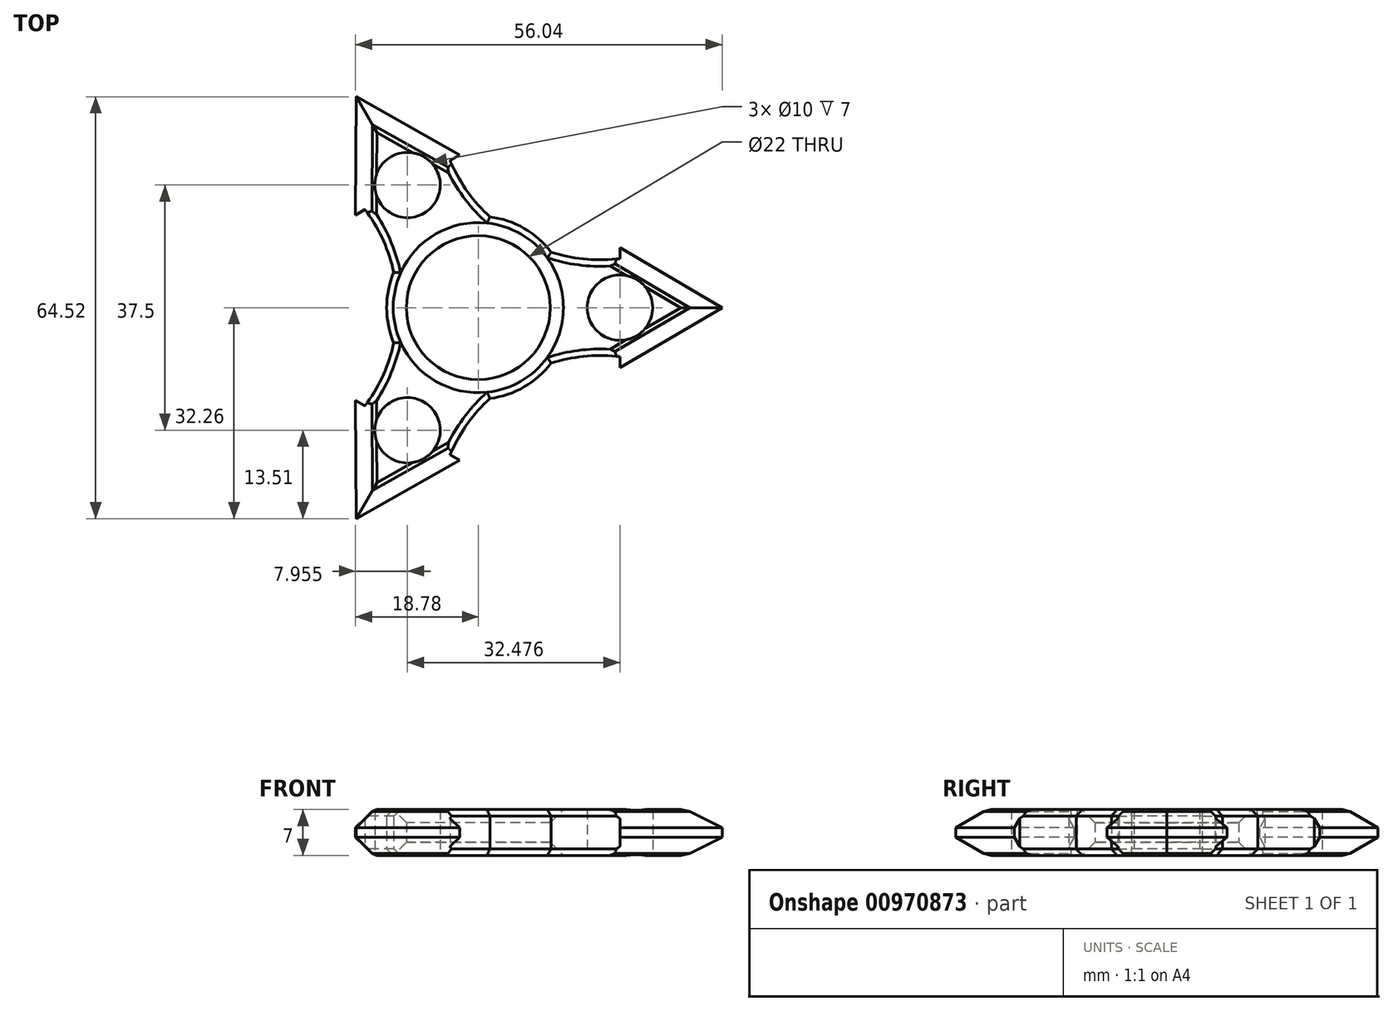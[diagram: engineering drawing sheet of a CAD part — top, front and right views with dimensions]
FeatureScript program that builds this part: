
annotation { "Feature Type Name" : "Feature", "Feature Type Description" : "" }
export const myFeature = defineFeature(function(context is Context, id is Id, definition is map)
    precondition{}
    {
        {
            var Q0;
            Q0=qCreatedBy(makeId("Top.planeOp"),FACE);
            var sketch = newSketch(context, id + "F0", { "sketchPlane" : qUnion([Q0])});
            skCircle(sketch, "E0.cCircle", {"center": v(0, 0) * mm, "radius": 17.32 * mm, "construction": true});
            skPoint(sketch, "E0.0.midPoint", {"position": v(-17.32, 0) * mm});
            skCircle(sketch, "E1", {"center": v(0, 0) * mm, "radius": 11 * mm});
            skLineSegment(sketch, "E2", {"start": v(-17.32, 30) * mm, "end": v(8.66, -15) * mm, "construction": true});
            skLineSegment(sketch, "E3", {"start": v(34.64, 0) * mm, "end": v(-17.32, 0) * mm, "construction": true});
            skLineSegment(sketch, "E4", {"start": v(8.66, 15) * mm, "end": v(-17.32, -30) * mm, "construction": true});
            skArc(sketch, "E5", {"start": v(8.66, 15) * mm, "mid": v(8.66, 15) * mm, "end": v(8.66, 15) * mm});
            skArc(sketch, "E6", {"start": v(-4.33, 22.5) * mm, "mid": v(-1.74, 17.87) * mm, "end": v(1.77, 13.89) * mm});
            skArc(sketch, "E7", {"start": v(-17.32, -15) * mm, "mid": v(-14.6, -10.44) * mm, "end": v(-12.91, -5.4) * mm});
            skArc(sketch, "E8", {"start": v(21.65, -7.5) * mm, "mid": v(16.34, -7.43) * mm, "end": v(11.14, -8.48) * mm});
            skCircle(sketch, "E9", {"center": v(0, 0) * mm, "radius": 14 * mm});
            skLineSegment(sketch, "E10", {"start": v(-10.83, 18.75) * mm, "end": v(-19.33, 33.47) * mm, "construction": true});
            skLineSegment(sketch, "E11", {"start": v(21.65, 0) * mm, "end": v(38.65, 0) * mm, "construction": true});
            skPoint(sketch, "E11.endSnap0", {"position": v(21.65, 0) * mm});
            skLineSegment(sketch, "E12", {"start": v(-10.83, -18.75) * mm, "end": v(-19.33, -33.47) * mm, "construction": true});
            skLineSegment(sketch, "E13", {"start": v(-4.33, 22.5) * mm, "end": v(-2.17, 23.75) * mm, "construction": true});
            skLineSegment(sketch, "E14", {"start": v(-17.32, 15) * mm, "end": v(-19.49, 13.75) * mm, "construction": true});
            skLineSegment(sketch, "E15", {"start": v(-17.32, -15) * mm, "end": v(-19.49, -13.75) * mm, "construction": true});
            skLineSegment(sketch, "E16", {"start": v(-4.33, -22.5) * mm, "end": v(-2.17, -23.75) * mm, "construction": true});
            skLineSegment(sketch, "E17", {"start": v(21.65, -7.5) * mm, "end": v(21.65, -10) * mm, "construction": true});
            skLineSegment(sketch, "E18", {"start": v(21.65, 7.5) * mm, "end": v(21.65, 10) * mm, "construction": true});
            skLineSegment(sketch, "E19", {"start": v(-19.33, 33.47) * mm, "end": v(-19.49, 13.75) * mm});
            skLineSegment(sketch, "E20", {"start": v(-2.17, 23.75) * mm, "end": v(-19.33, 33.47) * mm});
            skLineSegment(sketch, "E21", {"start": v(-19.49, -13.75) * mm, "end": v(-19.33, -33.47) * mm});
            skLineSegment(sketch, "E22", {"start": v(-2.17, -23.75) * mm, "end": v(-19.33, -33.47) * mm});
            skLineSegment(sketch, "E23", {"start": v(-19.49, -13.75) * mm, "end": v(-17.32, -15) * mm});
            skLineSegment(sketch, "E24", {"start": v(21.65, -10) * mm, "end": v(38.65, 0) * mm});
            skLineSegment(sketch, "E25", {"start": v(21.65, 10) * mm, "end": v(38.65, 0) * mm});
            skLineSegment(sketch, "E26", {"start": v(21.65, 10) * mm, "end": v(21.65, 7.5) * mm});
            skLineSegment(sketch, "E27", {"start": v(-19.49, 13.75) * mm, "end": v(-17.32, 15) * mm});
            skPoint(sketch, "E0.2.start.orphan", {"position": v(34.64, 0) * mm});
            skArc(sketch, "E28.trimOffspring", {"start": v(-12.91, 5.4) * mm, "mid": v(-14.6, 10.44) * mm, "end": v(-17.32, 15) * mm});
            skArc(sketch, "E29.trimOffspring", {"start": v(1.77, -13.89) * mm, "mid": v(-1.74, -17.87) * mm, "end": v(-4.33, -22.5) * mm});
            skArc(sketch, "E30.trimOffspring", {"start": v(11.14, 8.48) * mm, "mid": v(16.34, 7.43) * mm, "end": v(21.65, 7.5) * mm});
            skLineSegment(sketch, "E31.trimOffspring", {"start": v(21.65, -7.5) * mm, "end": v(21.65, -10) * mm});
            skLineSegment(sketch, "E32.trimOffspring", {"start": v(-4.33, -22.5) * mm, "end": v(-2.17, -23.75) * mm});
            skLineSegment(sketch, "E33.trimOffspring", {"start": v(-4.33, 22.5) * mm, "end": v(-2.17, 23.75) * mm});
            skCircle(sketch, "E34", {"center": v(-10.83, 18.75) * mm, "radius": 5 * mm});
            skCircle(sketch, "E35", {"center": v(21.65, 0) * mm, "radius": 5 * mm});
            skCircle(sketch, "E36", {"center": v(-10.83, -18.75) * mm, "radius": 5 * mm});
            skSolve(sketch);
        }
        {
            var Q0;
            Q0=qSketchRegion(id+"F0",true);
            extrude(context, id + "F1", {"entities" : qUnion([Q0]), "depth" : 7 * mm, "offsetDistance" : 25 * mm});
        }
        {
            var Q0;
            Q0=makeQuery(id+"F1.opExtrude","CAP_EDGE",EDGE,{"disambiguationData":[OSD([sQuery(id+"F0.wireOp",EDGE,"E24")])],"isStart":false});
            var Q1;
            Q1=makeQuery(id+"F1.opExtrude","CAP_EDGE",EDGE,{"disambiguationData":[OSD([sQuery(id+"F0.wireOp",EDGE,"E24")])],"isStart":true});
            var Q2;
            Q2=makeQuery(id+"F1.opExtrude","CAP_EDGE",EDGE,{"disambiguationData":[OSD([sQuery(id+"F0.wireOp",EDGE,"E25")])],"isStart":true});
            var Q3;
            Q3=makeQuery(id+"F1.opExtrude","CAP_EDGE",EDGE,{"disambiguationData":[OSD([sQuery(id+"F0.wireOp",EDGE,"E25")])],"isStart":false});
            var Q4;
            Q4=makeQuery(id+"F1.opExtrude","CAP_EDGE",EDGE,{"disambiguationData":[OSD([sQuery(id+"F0.wireOp",EDGE,"E20")])],"isStart":false});
            var Q5;
            Q5=makeQuery(id+"F1.opExtrude","CAP_EDGE",EDGE,{"disambiguationData":[OSD([sQuery(id+"F0.wireOp",EDGE,"E19")])],"isStart":false});
            var Q6;
            Q6=makeQuery(id+"F1.opExtrude","CAP_EDGE",EDGE,{"disambiguationData":[OSD([sQuery(id+"F0.wireOp",EDGE,"E19")])],"isStart":true});
            var Q7;
            Q7=makeQuery(id+"F1.opExtrude","CAP_EDGE",EDGE,{"disambiguationData":[OSD([sQuery(id+"F0.wireOp",EDGE,"E20")])],"isStart":true});
            var Q8;
            Q8=makeQuery(id+"F1.opExtrude","CAP_EDGE",EDGE,{"disambiguationData":[OSD([sQuery(id+"F0.wireOp",EDGE,"E22")])],"isStart":false});
            var Q9;
            Q9=makeQuery(id+"F1.opExtrude","CAP_EDGE",EDGE,{"disambiguationData":[OSD([sQuery(id+"F0.wireOp",EDGE,"E22")])],"isStart":true});
            var Q10;
            Q10=makeQuery(id+"F1.opExtrude","CAP_EDGE",EDGE,{"disambiguationData":[OSD([sQuery(id+"F0.wireOp",EDGE,"E21")])],"isStart":true});
            var Q11;
            Q11=makeQuery(id+"F1.opExtrude","CAP_EDGE",EDGE,{"disambiguationData":[OSD([sQuery(id+"F0.wireOp",EDGE,"E21")])],"isStart":false});
            chamfer(context, id + "F2", {"entities" : qUnion([Q0, Q1, Q2, Q3, Q4, Q5, Q6, Q7, Q8, Q9, Q10, Q11]), "width" : 3.5 * mm, "tangentPropagation" : true});
        }
        {
            var Q0;
            Q0=makeQuery(id+"F1.opExtrude","CAP_EDGE",EDGE,{"disambiguationData":[OSD([sQuery(id+"F0.wireOp",EDGE,"E1")])],"isStart":false});
            var Q1;
            Q1=makeQuery(id+"F1.opExtrude","CAP_EDGE",EDGE,{"disambiguationData":[OSD([sQuery(id+"F0.wireOp",EDGE,"E1")])],"isStart":true});
            chamfer(context, id + "F3", {"entities" : qUnion([Q0, Q1]), "width" : 2 * mm, "tangentPropagation" : true});
        }
        {
            var Q0;
            {var subQ0=sQuery(id+"F0.wireOp",EDGE,"E9");Q0=makeQuery(id+"F1.opExtrude","CAP_EDGE",EDGE,{"disambiguationData":[OSD([subQ0]),TDD([makeQuery(id+"F0.imprint","IMPRINT",EDGE,{"disambiguationData":[TD([[makeQuery(id+"F0.imprint","INTERSECT",VERTEX,{"derivedFrom":[sQuery(id+"F0.wireOp",EDGE,"E6"),subQ0]}),1.0]])],"derivedFrom":subQ0})])],"isStart":true});}
            var Q1;
            {var subQ0=sQuery(id+"F0.wireOp",EDGE,"E9");Q1=makeQuery(id+"F1.opExtrude","CAP_EDGE",EDGE,{"disambiguationData":[OSD([subQ0]),TDD([makeQuery(id+"F0.imprint","IMPRINT",EDGE,{"disambiguationData":[TD([[makeQuery(id+"F0.imprint","INTERSECT",VERTEX,{"derivedFrom":[sQuery(id+"F0.wireOp",EDGE,"E6"),subQ0]}),1.0]])],"derivedFrom":subQ0})])],"isStart":false});}
            var Q2;
            {var subQ0=sQuery(id+"F0.wireOp",EDGE,"E9");Q2=makeQuery(id+"F1.opExtrude","CAP_EDGE",EDGE,{"disambiguationData":[OSD([subQ0]),TDD([makeQuery(id+"F0.imprint","IMPRINT",EDGE,{"disambiguationData":[TD([[makeQuery(id+"F0.imprint","INTERSECT",VERTEX,{"derivedFrom":[sQuery(id+"F0.wireOp",EDGE,"E8"),subQ0]}),1.0]])],"derivedFrom":subQ0})])],"isStart":false});}
            var Q3;
            {var subQ0=sQuery(id+"F0.wireOp",EDGE,"E9");Q3=makeQuery(id+"F1.opExtrude","CAP_EDGE",EDGE,{"disambiguationData":[OSD([subQ0]),TDD([makeQuery(id+"F0.imprint","IMPRINT",EDGE,{"disambiguationData":[TD([[makeQuery(id+"F0.imprint","INTERSECT",VERTEX,{"derivedFrom":[sQuery(id+"F0.wireOp",EDGE,"E8"),subQ0]}),1.0]])],"derivedFrom":subQ0})])],"isStart":true});}
            var Q4;
            {var subQ0=sQuery(id+"F0.wireOp",EDGE,"E9");Q4=makeQuery(id+"F1.opExtrude","CAP_EDGE",EDGE,{"disambiguationData":[OSD([subQ0]),TDD([makeQuery(id+"F0.imprint","IMPRINT",EDGE,{"disambiguationData":[TD([[makeQuery(id+"F0.imprint","INTERSECT",VERTEX,{"derivedFrom":[sQuery(id+"F0.wireOp",EDGE,"E7"),subQ0]}),1.0]])],"derivedFrom":subQ0})])],"isStart":false});}
            var Q5;
            {var subQ0=sQuery(id+"F0.wireOp",EDGE,"E9");Q5=makeQuery(id+"F1.opExtrude","CAP_EDGE",EDGE,{"disambiguationData":[OSD([subQ0]),TDD([makeQuery(id+"F0.imprint","IMPRINT",EDGE,{"disambiguationData":[TD([[makeQuery(id+"F0.imprint","INTERSECT",VERTEX,{"derivedFrom":[sQuery(id+"F0.wireOp",EDGE,"E7"),subQ0]}),1.0]])],"derivedFrom":subQ0})])],"isStart":true});}
            var Q6;
            Q6=makeQuery(id+"F1.opExtrude","CAP_EDGE",EDGE,{"disambiguationData":[OSD([sQuery(id+"F0.wireOp",EDGE,"E7")])],"isStart":false});
            var Q7;
            Q7=makeQuery(id+"F1.opExtrude","CAP_EDGE",EDGE,{"disambiguationData":[OSD([sQuery(id+"F0.wireOp",EDGE,"E7")])],"isStart":true});
            var Q8;
            Q8=makeQuery(id+"F1.opExtrude","CAP_EDGE",EDGE,{"disambiguationData":[OSD([sQuery(id+"F0.wireOp",EDGE,"E6")])],"isStart":false});
            var Q9;
            Q9=makeQuery(id+"F1.opExtrude","CAP_EDGE",EDGE,{"disambiguationData":[OSD([sQuery(id+"F0.wireOp",EDGE,"E6")])],"isStart":true});
            var Q10;
            Q10=makeQuery(id+"F1.opExtrude","CAP_EDGE",EDGE,{"disambiguationData":[OSD([sQuery(id+"F0.wireOp",EDGE,"E28.trimOffspring")])],"isStart":false});
            var Q11;
            Q11=makeQuery(id+"F1.opExtrude","CAP_EDGE",EDGE,{"disambiguationData":[OSD([sQuery(id+"F0.wireOp",EDGE,"E28.trimOffspring")])],"isStart":true});
            var Q12;
            Q12=makeQuery(id+"F1.opExtrude","CAP_EDGE",EDGE,{"disambiguationData":[OSD([sQuery(id+"F0.wireOp",EDGE,"E30.trimOffspring")])],"isStart":true});
            var Q13;
            Q13=makeQuery(id+"F1.opExtrude","CAP_EDGE",EDGE,{"disambiguationData":[OSD([sQuery(id+"F0.wireOp",EDGE,"E30.trimOffspring")])],"isStart":false});
            var Q14;
            Q14=makeQuery(id+"F1.opExtrude","CAP_EDGE",EDGE,{"disambiguationData":[OSD([sQuery(id+"F0.wireOp",EDGE,"E8")])],"isStart":false});
            var Q15;
            Q15=makeQuery(id+"F1.opExtrude","CAP_EDGE",EDGE,{"disambiguationData":[OSD([sQuery(id+"F0.wireOp",EDGE,"E8")])],"isStart":true});
            var Q16;
            {var subQ0=sQuery(id+"F0.wireOp",EDGE,"E24");Q16=makeQuery(id+"F2.opChamfer","BLEND_EDGE",EDGE,{"blendedFrom":[makeQuery(id+"F1.opExtrude","CAP_EDGE",EDGE,{"disambiguationData":[OSD([subQ0])],"isStart":true}),makeQuery(id+"F1.opExtrude","CAP_EDGE",EDGE,{"disambiguationData":[OSD([subQ0])],"isStart":false})],"blendedInto":[]});}
            var Q17;
            {var subQ0=sQuery(id+"F0.wireOp",EDGE,"E24");Q17=makeQuery(id+"F2.opChamfer","BLEND_EDGE",EDGE,{"blendedFrom":[makeQuery(id+"F1.opExtrude","CAP_EDGE",EDGE,{"disambiguationData":[OSD([subQ0])],"isStart":true}),makeQuery(id+"F1.opExtrude","CAP_FACE",FACE,{"disambiguationData":[OSD([sQuery(id+"F0.wireOp",EDGE,"E1"),sQuery(id+"F0.wireOp",EDGE,"E6"),sQuery(id+"F0.wireOp",EDGE,"E7"),sQuery(id+"F0.wireOp",EDGE,"E8"),sQuery(id+"F0.wireOp",EDGE,"E9"),sQuery(id+"F0.wireOp",EDGE,"E19"),sQuery(id+"F0.wireOp",EDGE,"E20"),sQuery(id+"F0.wireOp",EDGE,"E21"),sQuery(id+"F0.wireOp",EDGE,"E22"),sQuery(id+"F0.wireOp",EDGE,"E23"),subQ0,sQuery(id+"F0.wireOp",EDGE,"E25"),sQuery(id+"F0.wireOp",EDGE,"E26"),sQuery(id+"F0.wireOp",EDGE,"E27"),sQuery(id+"F0.wireOp",EDGE,"E28.trimOffspring"),sQuery(id+"F0.wireOp",EDGE,"E29.trimOffspring"),sQuery(id+"F0.wireOp",EDGE,"E30.trimOffspring"),sQuery(id+"F0.wireOp",EDGE,"E31.trimOffspring"),sQuery(id+"F0.wireOp",EDGE,"E32.trimOffspring"),sQuery(id+"F0.wireOp",EDGE,"E33.trimOffspring"),sQuery(id+"F0.wireOp",EDGE,"E34"),sQuery(id+"F0.wireOp",EDGE,"E35"),sQuery(id+"F0.wireOp",EDGE,"E36")])],"isStart":true})],"blendedInto":[makeQuery(id+"F1.opExtrude","CAP_FACE",FACE,{"disambiguationData":[OSD([sQuery(id+"F0.wireOp",EDGE,"E1"),sQuery(id+"F0.wireOp",EDGE,"E6"),sQuery(id+"F0.wireOp",EDGE,"E7"),sQuery(id+"F0.wireOp",EDGE,"E8"),sQuery(id+"F0.wireOp",EDGE,"E9"),sQuery(id+"F0.wireOp",EDGE,"E19"),sQuery(id+"F0.wireOp",EDGE,"E20"),sQuery(id+"F0.wireOp",EDGE,"E21"),sQuery(id+"F0.wireOp",EDGE,"E22"),sQuery(id+"F0.wireOp",EDGE,"E23"),subQ0,sQuery(id+"F0.wireOp",EDGE,"E25"),sQuery(id+"F0.wireOp",EDGE,"E26"),sQuery(id+"F0.wireOp",EDGE,"E27"),sQuery(id+"F0.wireOp",EDGE,"E28.trimOffspring"),sQuery(id+"F0.wireOp",EDGE,"E29.trimOffspring"),sQuery(id+"F0.wireOp",EDGE,"E30.trimOffspring"),sQuery(id+"F0.wireOp",EDGE,"E31.trimOffspring"),sQuery(id+"F0.wireOp",EDGE,"E32.trimOffspring"),sQuery(id+"F0.wireOp",EDGE,"E33.trimOffspring"),sQuery(id+"F0.wireOp",EDGE,"E34"),sQuery(id+"F0.wireOp",EDGE,"E35"),sQuery(id+"F0.wireOp",EDGE,"E36")])],"isStart":true})]});}
            var Q18;
            {var subQ0=sQuery(id+"F0.wireOp",EDGE,"E24");Q18=makeQuery(id+"F2.opChamfer","BLEND_EDGE",EDGE,{"blendedFrom":[makeQuery(id+"F1.opExtrude","CAP_EDGE",EDGE,{"disambiguationData":[OSD([subQ0])],"isStart":false}),makeQuery(id+"F1.opExtrude","CAP_FACE",FACE,{"disambiguationData":[OSD([sQuery(id+"F0.wireOp",EDGE,"E1"),sQuery(id+"F0.wireOp",EDGE,"E6"),sQuery(id+"F0.wireOp",EDGE,"E7"),sQuery(id+"F0.wireOp",EDGE,"E8"),sQuery(id+"F0.wireOp",EDGE,"E9"),sQuery(id+"F0.wireOp",EDGE,"E19"),sQuery(id+"F0.wireOp",EDGE,"E20"),sQuery(id+"F0.wireOp",EDGE,"E21"),sQuery(id+"F0.wireOp",EDGE,"E22"),sQuery(id+"F0.wireOp",EDGE,"E23"),subQ0,sQuery(id+"F0.wireOp",EDGE,"E25"),sQuery(id+"F0.wireOp",EDGE,"E26"),sQuery(id+"F0.wireOp",EDGE,"E27"),sQuery(id+"F0.wireOp",EDGE,"E28.trimOffspring"),sQuery(id+"F0.wireOp",EDGE,"E29.trimOffspring"),sQuery(id+"F0.wireOp",EDGE,"E30.trimOffspring"),sQuery(id+"F0.wireOp",EDGE,"E31.trimOffspring"),sQuery(id+"F0.wireOp",EDGE,"E32.trimOffspring"),sQuery(id+"F0.wireOp",EDGE,"E33.trimOffspring"),sQuery(id+"F0.wireOp",EDGE,"E34"),sQuery(id+"F0.wireOp",EDGE,"E35"),sQuery(id+"F0.wireOp",EDGE,"E36")])],"isStart":false})],"blendedInto":[makeQuery(id+"F1.opExtrude","CAP_FACE",FACE,{"disambiguationData":[OSD([sQuery(id+"F0.wireOp",EDGE,"E1"),sQuery(id+"F0.wireOp",EDGE,"E6"),sQuery(id+"F0.wireOp",EDGE,"E7"),sQuery(id+"F0.wireOp",EDGE,"E8"),sQuery(id+"F0.wireOp",EDGE,"E9"),sQuery(id+"F0.wireOp",EDGE,"E19"),sQuery(id+"F0.wireOp",EDGE,"E20"),sQuery(id+"F0.wireOp",EDGE,"E21"),sQuery(id+"F0.wireOp",EDGE,"E22"),sQuery(id+"F0.wireOp",EDGE,"E23"),subQ0,sQuery(id+"F0.wireOp",EDGE,"E25"),sQuery(id+"F0.wireOp",EDGE,"E26"),sQuery(id+"F0.wireOp",EDGE,"E27"),sQuery(id+"F0.wireOp",EDGE,"E28.trimOffspring"),sQuery(id+"F0.wireOp",EDGE,"E29.trimOffspring"),sQuery(id+"F0.wireOp",EDGE,"E30.trimOffspring"),sQuery(id+"F0.wireOp",EDGE,"E31.trimOffspring"),sQuery(id+"F0.wireOp",EDGE,"E32.trimOffspring"),sQuery(id+"F0.wireOp",EDGE,"E33.trimOffspring"),sQuery(id+"F0.wireOp",EDGE,"E34"),sQuery(id+"F0.wireOp",EDGE,"E35"),sQuery(id+"F0.wireOp",EDGE,"E36")])],"isStart":false})]});}
            var Q19;
            {var subQ0=sQuery(id+"F0.wireOp",EDGE,"E25");Q19=makeQuery(id+"F2.opChamfer","BLEND_EDGE",EDGE,{"blendedFrom":[makeQuery(id+"F1.opExtrude","CAP_EDGE",EDGE,{"disambiguationData":[OSD([subQ0])],"isStart":false}),makeQuery(id+"F1.opExtrude","CAP_FACE",FACE,{"disambiguationData":[OSD([sQuery(id+"F0.wireOp",EDGE,"E1"),sQuery(id+"F0.wireOp",EDGE,"E6"),sQuery(id+"F0.wireOp",EDGE,"E7"),sQuery(id+"F0.wireOp",EDGE,"E8"),sQuery(id+"F0.wireOp",EDGE,"E9"),sQuery(id+"F0.wireOp",EDGE,"E19"),sQuery(id+"F0.wireOp",EDGE,"E20"),sQuery(id+"F0.wireOp",EDGE,"E21"),sQuery(id+"F0.wireOp",EDGE,"E22"),sQuery(id+"F0.wireOp",EDGE,"E23"),sQuery(id+"F0.wireOp",EDGE,"E24"),subQ0,sQuery(id+"F0.wireOp",EDGE,"E26"),sQuery(id+"F0.wireOp",EDGE,"E27"),sQuery(id+"F0.wireOp",EDGE,"E28.trimOffspring"),sQuery(id+"F0.wireOp",EDGE,"E29.trimOffspring"),sQuery(id+"F0.wireOp",EDGE,"E30.trimOffspring"),sQuery(id+"F0.wireOp",EDGE,"E31.trimOffspring"),sQuery(id+"F0.wireOp",EDGE,"E32.trimOffspring"),sQuery(id+"F0.wireOp",EDGE,"E33.trimOffspring"),sQuery(id+"F0.wireOp",EDGE,"E34"),sQuery(id+"F0.wireOp",EDGE,"E35"),sQuery(id+"F0.wireOp",EDGE,"E36")])],"isStart":false})],"blendedInto":[makeQuery(id+"F1.opExtrude","CAP_FACE",FACE,{"disambiguationData":[OSD([sQuery(id+"F0.wireOp",EDGE,"E1"),sQuery(id+"F0.wireOp",EDGE,"E6"),sQuery(id+"F0.wireOp",EDGE,"E7"),sQuery(id+"F0.wireOp",EDGE,"E8"),sQuery(id+"F0.wireOp",EDGE,"E9"),sQuery(id+"F0.wireOp",EDGE,"E19"),sQuery(id+"F0.wireOp",EDGE,"E20"),sQuery(id+"F0.wireOp",EDGE,"E21"),sQuery(id+"F0.wireOp",EDGE,"E22"),sQuery(id+"F0.wireOp",EDGE,"E23"),sQuery(id+"F0.wireOp",EDGE,"E24"),subQ0,sQuery(id+"F0.wireOp",EDGE,"E26"),sQuery(id+"F0.wireOp",EDGE,"E27"),sQuery(id+"F0.wireOp",EDGE,"E28.trimOffspring"),sQuery(id+"F0.wireOp",EDGE,"E29.trimOffspring"),sQuery(id+"F0.wireOp",EDGE,"E30.trimOffspring"),sQuery(id+"F0.wireOp",EDGE,"E31.trimOffspring"),sQuery(id+"F0.wireOp",EDGE,"E32.trimOffspring"),sQuery(id+"F0.wireOp",EDGE,"E33.trimOffspring"),sQuery(id+"F0.wireOp",EDGE,"E34"),sQuery(id+"F0.wireOp",EDGE,"E35"),sQuery(id+"F0.wireOp",EDGE,"E36")])],"isStart":false})]});}
            var Q20;
            {var subQ0=sQuery(id+"F0.wireOp",EDGE,"E25");Q20=makeQuery(id+"F2.opChamfer","BLEND_EDGE",EDGE,{"blendedFrom":[makeQuery(id+"F1.opExtrude","CAP_EDGE",EDGE,{"disambiguationData":[OSD([subQ0])],"isStart":true}),makeQuery(id+"F1.opExtrude","CAP_EDGE",EDGE,{"disambiguationData":[OSD([subQ0])],"isStart":false})],"blendedInto":[]});}
            var Q21;
            {var subQ0=sQuery(id+"F0.wireOp",EDGE,"E25");Q21=makeQuery(id+"F2.opChamfer","BLEND_EDGE",EDGE,{"blendedFrom":[makeQuery(id+"F1.opExtrude","CAP_EDGE",EDGE,{"disambiguationData":[OSD([subQ0])],"isStart":true}),makeQuery(id+"F1.opExtrude","CAP_FACE",FACE,{"disambiguationData":[OSD([sQuery(id+"F0.wireOp",EDGE,"E1"),sQuery(id+"F0.wireOp",EDGE,"E6"),sQuery(id+"F0.wireOp",EDGE,"E7"),sQuery(id+"F0.wireOp",EDGE,"E8"),sQuery(id+"F0.wireOp",EDGE,"E9"),sQuery(id+"F0.wireOp",EDGE,"E19"),sQuery(id+"F0.wireOp",EDGE,"E20"),sQuery(id+"F0.wireOp",EDGE,"E21"),sQuery(id+"F0.wireOp",EDGE,"E22"),sQuery(id+"F0.wireOp",EDGE,"E23"),sQuery(id+"F0.wireOp",EDGE,"E24"),subQ0,sQuery(id+"F0.wireOp",EDGE,"E26"),sQuery(id+"F0.wireOp",EDGE,"E27"),sQuery(id+"F0.wireOp",EDGE,"E28.trimOffspring"),sQuery(id+"F0.wireOp",EDGE,"E29.trimOffspring"),sQuery(id+"F0.wireOp",EDGE,"E30.trimOffspring"),sQuery(id+"F0.wireOp",EDGE,"E31.trimOffspring"),sQuery(id+"F0.wireOp",EDGE,"E32.trimOffspring"),sQuery(id+"F0.wireOp",EDGE,"E33.trimOffspring"),sQuery(id+"F0.wireOp",EDGE,"E34"),sQuery(id+"F0.wireOp",EDGE,"E35"),sQuery(id+"F0.wireOp",EDGE,"E36")])],"isStart":true})],"blendedInto":[makeQuery(id+"F1.opExtrude","CAP_FACE",FACE,{"disambiguationData":[OSD([sQuery(id+"F0.wireOp",EDGE,"E1"),sQuery(id+"F0.wireOp",EDGE,"E6"),sQuery(id+"F0.wireOp",EDGE,"E7"),sQuery(id+"F0.wireOp",EDGE,"E8"),sQuery(id+"F0.wireOp",EDGE,"E9"),sQuery(id+"F0.wireOp",EDGE,"E19"),sQuery(id+"F0.wireOp",EDGE,"E20"),sQuery(id+"F0.wireOp",EDGE,"E21"),sQuery(id+"F0.wireOp",EDGE,"E22"),sQuery(id+"F0.wireOp",EDGE,"E23"),sQuery(id+"F0.wireOp",EDGE,"E24"),subQ0,sQuery(id+"F0.wireOp",EDGE,"E26"),sQuery(id+"F0.wireOp",EDGE,"E27"),sQuery(id+"F0.wireOp",EDGE,"E28.trimOffspring"),sQuery(id+"F0.wireOp",EDGE,"E29.trimOffspring"),sQuery(id+"F0.wireOp",EDGE,"E30.trimOffspring"),sQuery(id+"F0.wireOp",EDGE,"E31.trimOffspring"),sQuery(id+"F0.wireOp",EDGE,"E32.trimOffspring"),sQuery(id+"F0.wireOp",EDGE,"E33.trimOffspring"),sQuery(id+"F0.wireOp",EDGE,"E34"),sQuery(id+"F0.wireOp",EDGE,"E35"),sQuery(id+"F0.wireOp",EDGE,"E36")])],"isStart":true})]});}
            var Q22;
            {var subQ0=sQuery(id+"F0.wireOp",EDGE,"E20");Q22=makeQuery(id+"F2.opChamfer","BLEND_EDGE",EDGE,{"blendedFrom":[makeQuery(id+"F1.opExtrude","CAP_EDGE",EDGE,{"disambiguationData":[OSD([subQ0])],"isStart":true}),makeQuery(id+"F1.opExtrude","CAP_FACE",FACE,{"disambiguationData":[OSD([sQuery(id+"F0.wireOp",EDGE,"E1"),sQuery(id+"F0.wireOp",EDGE,"E6"),sQuery(id+"F0.wireOp",EDGE,"E7"),sQuery(id+"F0.wireOp",EDGE,"E8"),sQuery(id+"F0.wireOp",EDGE,"E9"),sQuery(id+"F0.wireOp",EDGE,"E19"),subQ0,sQuery(id+"F0.wireOp",EDGE,"E21"),sQuery(id+"F0.wireOp",EDGE,"E22"),sQuery(id+"F0.wireOp",EDGE,"E23"),sQuery(id+"F0.wireOp",EDGE,"E24"),sQuery(id+"F0.wireOp",EDGE,"E25"),sQuery(id+"F0.wireOp",EDGE,"E26"),sQuery(id+"F0.wireOp",EDGE,"E27"),sQuery(id+"F0.wireOp",EDGE,"E28.trimOffspring"),sQuery(id+"F0.wireOp",EDGE,"E29.trimOffspring"),sQuery(id+"F0.wireOp",EDGE,"E30.trimOffspring"),sQuery(id+"F0.wireOp",EDGE,"E31.trimOffspring"),sQuery(id+"F0.wireOp",EDGE,"E32.trimOffspring"),sQuery(id+"F0.wireOp",EDGE,"E33.trimOffspring"),sQuery(id+"F0.wireOp",EDGE,"E34"),sQuery(id+"F0.wireOp",EDGE,"E35"),sQuery(id+"F0.wireOp",EDGE,"E36")])],"isStart":true})],"blendedInto":[makeQuery(id+"F1.opExtrude","CAP_FACE",FACE,{"disambiguationData":[OSD([sQuery(id+"F0.wireOp",EDGE,"E1"),sQuery(id+"F0.wireOp",EDGE,"E6"),sQuery(id+"F0.wireOp",EDGE,"E7"),sQuery(id+"F0.wireOp",EDGE,"E8"),sQuery(id+"F0.wireOp",EDGE,"E9"),sQuery(id+"F0.wireOp",EDGE,"E19"),subQ0,sQuery(id+"F0.wireOp",EDGE,"E21"),sQuery(id+"F0.wireOp",EDGE,"E22"),sQuery(id+"F0.wireOp",EDGE,"E23"),sQuery(id+"F0.wireOp",EDGE,"E24"),sQuery(id+"F0.wireOp",EDGE,"E25"),sQuery(id+"F0.wireOp",EDGE,"E26"),sQuery(id+"F0.wireOp",EDGE,"E27"),sQuery(id+"F0.wireOp",EDGE,"E28.trimOffspring"),sQuery(id+"F0.wireOp",EDGE,"E29.trimOffspring"),sQuery(id+"F0.wireOp",EDGE,"E30.trimOffspring"),sQuery(id+"F0.wireOp",EDGE,"E31.trimOffspring"),sQuery(id+"F0.wireOp",EDGE,"E32.trimOffspring"),sQuery(id+"F0.wireOp",EDGE,"E33.trimOffspring"),sQuery(id+"F0.wireOp",EDGE,"E34"),sQuery(id+"F0.wireOp",EDGE,"E35"),sQuery(id+"F0.wireOp",EDGE,"E36")])],"isStart":true})]});}
            var Q23;
            {var subQ0=sQuery(id+"F0.wireOp",EDGE,"E20");Q23=makeQuery(id+"F2.opChamfer","BLEND_EDGE",EDGE,{"blendedFrom":[makeQuery(id+"F1.opExtrude","CAP_EDGE",EDGE,{"disambiguationData":[OSD([subQ0])],"isStart":true}),makeQuery(id+"F1.opExtrude","CAP_EDGE",EDGE,{"disambiguationData":[OSD([subQ0])],"isStart":false})],"blendedInto":[]});}
            var Q24;
            {var subQ0=sQuery(id+"F0.wireOp",EDGE,"E20");Q24=makeQuery(id+"F2.opChamfer","BLEND_EDGE",EDGE,{"blendedFrom":[makeQuery(id+"F1.opExtrude","CAP_EDGE",EDGE,{"disambiguationData":[OSD([subQ0])],"isStart":false}),makeQuery(id+"F1.opExtrude","CAP_FACE",FACE,{"disambiguationData":[OSD([sQuery(id+"F0.wireOp",EDGE,"E1"),sQuery(id+"F0.wireOp",EDGE,"E6"),sQuery(id+"F0.wireOp",EDGE,"E7"),sQuery(id+"F0.wireOp",EDGE,"E8"),sQuery(id+"F0.wireOp",EDGE,"E9"),sQuery(id+"F0.wireOp",EDGE,"E19"),subQ0,sQuery(id+"F0.wireOp",EDGE,"E21"),sQuery(id+"F0.wireOp",EDGE,"E22"),sQuery(id+"F0.wireOp",EDGE,"E23"),sQuery(id+"F0.wireOp",EDGE,"E24"),sQuery(id+"F0.wireOp",EDGE,"E25"),sQuery(id+"F0.wireOp",EDGE,"E26"),sQuery(id+"F0.wireOp",EDGE,"E27"),sQuery(id+"F0.wireOp",EDGE,"E28.trimOffspring"),sQuery(id+"F0.wireOp",EDGE,"E29.trimOffspring"),sQuery(id+"F0.wireOp",EDGE,"E30.trimOffspring"),sQuery(id+"F0.wireOp",EDGE,"E31.trimOffspring"),sQuery(id+"F0.wireOp",EDGE,"E32.trimOffspring"),sQuery(id+"F0.wireOp",EDGE,"E33.trimOffspring"),sQuery(id+"F0.wireOp",EDGE,"E34"),sQuery(id+"F0.wireOp",EDGE,"E35"),sQuery(id+"F0.wireOp",EDGE,"E36")])],"isStart":false})],"blendedInto":[makeQuery(id+"F1.opExtrude","CAP_FACE",FACE,{"disambiguationData":[OSD([sQuery(id+"F0.wireOp",EDGE,"E1"),sQuery(id+"F0.wireOp",EDGE,"E6"),sQuery(id+"F0.wireOp",EDGE,"E7"),sQuery(id+"F0.wireOp",EDGE,"E8"),sQuery(id+"F0.wireOp",EDGE,"E9"),sQuery(id+"F0.wireOp",EDGE,"E19"),subQ0,sQuery(id+"F0.wireOp",EDGE,"E21"),sQuery(id+"F0.wireOp",EDGE,"E22"),sQuery(id+"F0.wireOp",EDGE,"E23"),sQuery(id+"F0.wireOp",EDGE,"E24"),sQuery(id+"F0.wireOp",EDGE,"E25"),sQuery(id+"F0.wireOp",EDGE,"E26"),sQuery(id+"F0.wireOp",EDGE,"E27"),sQuery(id+"F0.wireOp",EDGE,"E28.trimOffspring"),sQuery(id+"F0.wireOp",EDGE,"E29.trimOffspring"),sQuery(id+"F0.wireOp",EDGE,"E30.trimOffspring"),sQuery(id+"F0.wireOp",EDGE,"E31.trimOffspring"),sQuery(id+"F0.wireOp",EDGE,"E32.trimOffspring"),sQuery(id+"F0.wireOp",EDGE,"E33.trimOffspring"),sQuery(id+"F0.wireOp",EDGE,"E34"),sQuery(id+"F0.wireOp",EDGE,"E35"),sQuery(id+"F0.wireOp",EDGE,"E36")])],"isStart":false})]});}
            var Q25;
            {var subQ0=sQuery(id+"F0.wireOp",EDGE,"E19");Q25=makeQuery(id+"F2.opChamfer","BLEND_EDGE",EDGE,{"blendedFrom":[makeQuery(id+"F1.opExtrude","CAP_EDGE",EDGE,{"disambiguationData":[OSD([subQ0])],"isStart":false}),makeQuery(id+"F1.opExtrude","CAP_FACE",FACE,{"disambiguationData":[OSD([sQuery(id+"F0.wireOp",EDGE,"E1"),sQuery(id+"F0.wireOp",EDGE,"E6"),sQuery(id+"F0.wireOp",EDGE,"E7"),sQuery(id+"F0.wireOp",EDGE,"E8"),sQuery(id+"F0.wireOp",EDGE,"E9"),subQ0,sQuery(id+"F0.wireOp",EDGE,"E20"),sQuery(id+"F0.wireOp",EDGE,"E21"),sQuery(id+"F0.wireOp",EDGE,"E22"),sQuery(id+"F0.wireOp",EDGE,"E23"),sQuery(id+"F0.wireOp",EDGE,"E24"),sQuery(id+"F0.wireOp",EDGE,"E25"),sQuery(id+"F0.wireOp",EDGE,"E26"),sQuery(id+"F0.wireOp",EDGE,"E27"),sQuery(id+"F0.wireOp",EDGE,"E28.trimOffspring"),sQuery(id+"F0.wireOp",EDGE,"E29.trimOffspring"),sQuery(id+"F0.wireOp",EDGE,"E30.trimOffspring"),sQuery(id+"F0.wireOp",EDGE,"E31.trimOffspring"),sQuery(id+"F0.wireOp",EDGE,"E32.trimOffspring"),sQuery(id+"F0.wireOp",EDGE,"E33.trimOffspring"),sQuery(id+"F0.wireOp",EDGE,"E34"),sQuery(id+"F0.wireOp",EDGE,"E35"),sQuery(id+"F0.wireOp",EDGE,"E36")])],"isStart":false})],"blendedInto":[makeQuery(id+"F1.opExtrude","CAP_FACE",FACE,{"disambiguationData":[OSD([sQuery(id+"F0.wireOp",EDGE,"E1"),sQuery(id+"F0.wireOp",EDGE,"E6"),sQuery(id+"F0.wireOp",EDGE,"E7"),sQuery(id+"F0.wireOp",EDGE,"E8"),sQuery(id+"F0.wireOp",EDGE,"E9"),subQ0,sQuery(id+"F0.wireOp",EDGE,"E20"),sQuery(id+"F0.wireOp",EDGE,"E21"),sQuery(id+"F0.wireOp",EDGE,"E22"),sQuery(id+"F0.wireOp",EDGE,"E23"),sQuery(id+"F0.wireOp",EDGE,"E24"),sQuery(id+"F0.wireOp",EDGE,"E25"),sQuery(id+"F0.wireOp",EDGE,"E26"),sQuery(id+"F0.wireOp",EDGE,"E27"),sQuery(id+"F0.wireOp",EDGE,"E28.trimOffspring"),sQuery(id+"F0.wireOp",EDGE,"E29.trimOffspring"),sQuery(id+"F0.wireOp",EDGE,"E30.trimOffspring"),sQuery(id+"F0.wireOp",EDGE,"E31.trimOffspring"),sQuery(id+"F0.wireOp",EDGE,"E32.trimOffspring"),sQuery(id+"F0.wireOp",EDGE,"E33.trimOffspring"),sQuery(id+"F0.wireOp",EDGE,"E34"),sQuery(id+"F0.wireOp",EDGE,"E35"),sQuery(id+"F0.wireOp",EDGE,"E36")])],"isStart":false})]});}
            var Q26;
            {var subQ0=sQuery(id+"F0.wireOp",EDGE,"E19");Q26=makeQuery(id+"F2.opChamfer","BLEND_EDGE",EDGE,{"blendedFrom":[makeQuery(id+"F1.opExtrude","CAP_EDGE",EDGE,{"disambiguationData":[OSD([subQ0])],"isStart":true}),makeQuery(id+"F1.opExtrude","CAP_EDGE",EDGE,{"disambiguationData":[OSD([subQ0])],"isStart":false})],"blendedInto":[]});}
            var Q27;
            {var subQ0=sQuery(id+"F0.wireOp",EDGE,"E19");Q27=makeQuery(id+"F2.opChamfer","BLEND_EDGE",EDGE,{"blendedFrom":[makeQuery(id+"F1.opExtrude","CAP_EDGE",EDGE,{"disambiguationData":[OSD([subQ0])],"isStart":true}),makeQuery(id+"F1.opExtrude","CAP_FACE",FACE,{"disambiguationData":[OSD([sQuery(id+"F0.wireOp",EDGE,"E1"),sQuery(id+"F0.wireOp",EDGE,"E6"),sQuery(id+"F0.wireOp",EDGE,"E7"),sQuery(id+"F0.wireOp",EDGE,"E8"),sQuery(id+"F0.wireOp",EDGE,"E9"),subQ0,sQuery(id+"F0.wireOp",EDGE,"E20"),sQuery(id+"F0.wireOp",EDGE,"E21"),sQuery(id+"F0.wireOp",EDGE,"E22"),sQuery(id+"F0.wireOp",EDGE,"E23"),sQuery(id+"F0.wireOp",EDGE,"E24"),sQuery(id+"F0.wireOp",EDGE,"E25"),sQuery(id+"F0.wireOp",EDGE,"E26"),sQuery(id+"F0.wireOp",EDGE,"E27"),sQuery(id+"F0.wireOp",EDGE,"E28.trimOffspring"),sQuery(id+"F0.wireOp",EDGE,"E29.trimOffspring"),sQuery(id+"F0.wireOp",EDGE,"E30.trimOffspring"),sQuery(id+"F0.wireOp",EDGE,"E31.trimOffspring"),sQuery(id+"F0.wireOp",EDGE,"E32.trimOffspring"),sQuery(id+"F0.wireOp",EDGE,"E33.trimOffspring"),sQuery(id+"F0.wireOp",EDGE,"E34"),sQuery(id+"F0.wireOp",EDGE,"E35"),sQuery(id+"F0.wireOp",EDGE,"E36")])],"isStart":true})],"blendedInto":[makeQuery(id+"F1.opExtrude","CAP_FACE",FACE,{"disambiguationData":[OSD([sQuery(id+"F0.wireOp",EDGE,"E1"),sQuery(id+"F0.wireOp",EDGE,"E6"),sQuery(id+"F0.wireOp",EDGE,"E7"),sQuery(id+"F0.wireOp",EDGE,"E8"),sQuery(id+"F0.wireOp",EDGE,"E9"),subQ0,sQuery(id+"F0.wireOp",EDGE,"E20"),sQuery(id+"F0.wireOp",EDGE,"E21"),sQuery(id+"F0.wireOp",EDGE,"E22"),sQuery(id+"F0.wireOp",EDGE,"E23"),sQuery(id+"F0.wireOp",EDGE,"E24"),sQuery(id+"F0.wireOp",EDGE,"E25"),sQuery(id+"F0.wireOp",EDGE,"E26"),sQuery(id+"F0.wireOp",EDGE,"E27"),sQuery(id+"F0.wireOp",EDGE,"E28.trimOffspring"),sQuery(id+"F0.wireOp",EDGE,"E29.trimOffspring"),sQuery(id+"F0.wireOp",EDGE,"E30.trimOffspring"),sQuery(id+"F0.wireOp",EDGE,"E31.trimOffspring"),sQuery(id+"F0.wireOp",EDGE,"E32.trimOffspring"),sQuery(id+"F0.wireOp",EDGE,"E33.trimOffspring"),sQuery(id+"F0.wireOp",EDGE,"E34"),sQuery(id+"F0.wireOp",EDGE,"E35"),sQuery(id+"F0.wireOp",EDGE,"E36")])],"isStart":true})]});}
            var Q28;
            {var subQ0=sQuery(id+"F0.wireOp",EDGE,"E21");Q28=makeQuery(id+"F2.opChamfer","BLEND_EDGE",EDGE,{"blendedFrom":[makeQuery(id+"F1.opExtrude","CAP_EDGE",EDGE,{"disambiguationData":[OSD([subQ0])],"isStart":true}),makeQuery(id+"F1.opExtrude","CAP_FACE",FACE,{"disambiguationData":[OSD([sQuery(id+"F0.wireOp",EDGE,"E1"),sQuery(id+"F0.wireOp",EDGE,"E6"),sQuery(id+"F0.wireOp",EDGE,"E7"),sQuery(id+"F0.wireOp",EDGE,"E8"),sQuery(id+"F0.wireOp",EDGE,"E9"),sQuery(id+"F0.wireOp",EDGE,"E19"),sQuery(id+"F0.wireOp",EDGE,"E20"),subQ0,sQuery(id+"F0.wireOp",EDGE,"E22"),sQuery(id+"F0.wireOp",EDGE,"E23"),sQuery(id+"F0.wireOp",EDGE,"E24"),sQuery(id+"F0.wireOp",EDGE,"E25"),sQuery(id+"F0.wireOp",EDGE,"E26"),sQuery(id+"F0.wireOp",EDGE,"E27"),sQuery(id+"F0.wireOp",EDGE,"E28.trimOffspring"),sQuery(id+"F0.wireOp",EDGE,"E29.trimOffspring"),sQuery(id+"F0.wireOp",EDGE,"E30.trimOffspring"),sQuery(id+"F0.wireOp",EDGE,"E31.trimOffspring"),sQuery(id+"F0.wireOp",EDGE,"E32.trimOffspring"),sQuery(id+"F0.wireOp",EDGE,"E33.trimOffspring"),sQuery(id+"F0.wireOp",EDGE,"E34"),sQuery(id+"F0.wireOp",EDGE,"E35"),sQuery(id+"F0.wireOp",EDGE,"E36")])],"isStart":true})],"blendedInto":[makeQuery(id+"F1.opExtrude","CAP_FACE",FACE,{"disambiguationData":[OSD([sQuery(id+"F0.wireOp",EDGE,"E1"),sQuery(id+"F0.wireOp",EDGE,"E6"),sQuery(id+"F0.wireOp",EDGE,"E7"),sQuery(id+"F0.wireOp",EDGE,"E8"),sQuery(id+"F0.wireOp",EDGE,"E9"),sQuery(id+"F0.wireOp",EDGE,"E19"),sQuery(id+"F0.wireOp",EDGE,"E20"),subQ0,sQuery(id+"F0.wireOp",EDGE,"E22"),sQuery(id+"F0.wireOp",EDGE,"E23"),sQuery(id+"F0.wireOp",EDGE,"E24"),sQuery(id+"F0.wireOp",EDGE,"E25"),sQuery(id+"F0.wireOp",EDGE,"E26"),sQuery(id+"F0.wireOp",EDGE,"E27"),sQuery(id+"F0.wireOp",EDGE,"E28.trimOffspring"),sQuery(id+"F0.wireOp",EDGE,"E29.trimOffspring"),sQuery(id+"F0.wireOp",EDGE,"E30.trimOffspring"),sQuery(id+"F0.wireOp",EDGE,"E31.trimOffspring"),sQuery(id+"F0.wireOp",EDGE,"E32.trimOffspring"),sQuery(id+"F0.wireOp",EDGE,"E33.trimOffspring"),sQuery(id+"F0.wireOp",EDGE,"E34"),sQuery(id+"F0.wireOp",EDGE,"E35"),sQuery(id+"F0.wireOp",EDGE,"E36")])],"isStart":true})]});}
            var Q29;
            {var subQ0=sQuery(id+"F0.wireOp",EDGE,"E21");Q29=makeQuery(id+"F2.opChamfer","BLEND_EDGE",EDGE,{"blendedFrom":[makeQuery(id+"F1.opExtrude","CAP_EDGE",EDGE,{"disambiguationData":[OSD([subQ0])],"isStart":true}),makeQuery(id+"F1.opExtrude","CAP_EDGE",EDGE,{"disambiguationData":[OSD([subQ0])],"isStart":false})],"blendedInto":[]});}
            var Q30;
            {var subQ0=sQuery(id+"F0.wireOp",EDGE,"E21");Q30=makeQuery(id+"F2.opChamfer","BLEND_EDGE",EDGE,{"blendedFrom":[makeQuery(id+"F1.opExtrude","CAP_EDGE",EDGE,{"disambiguationData":[OSD([subQ0])],"isStart":false}),makeQuery(id+"F1.opExtrude","CAP_FACE",FACE,{"disambiguationData":[OSD([sQuery(id+"F0.wireOp",EDGE,"E1"),sQuery(id+"F0.wireOp",EDGE,"E6"),sQuery(id+"F0.wireOp",EDGE,"E7"),sQuery(id+"F0.wireOp",EDGE,"E8"),sQuery(id+"F0.wireOp",EDGE,"E9"),sQuery(id+"F0.wireOp",EDGE,"E19"),sQuery(id+"F0.wireOp",EDGE,"E20"),subQ0,sQuery(id+"F0.wireOp",EDGE,"E22"),sQuery(id+"F0.wireOp",EDGE,"E23"),sQuery(id+"F0.wireOp",EDGE,"E24"),sQuery(id+"F0.wireOp",EDGE,"E25"),sQuery(id+"F0.wireOp",EDGE,"E26"),sQuery(id+"F0.wireOp",EDGE,"E27"),sQuery(id+"F0.wireOp",EDGE,"E28.trimOffspring"),sQuery(id+"F0.wireOp",EDGE,"E29.trimOffspring"),sQuery(id+"F0.wireOp",EDGE,"E30.trimOffspring"),sQuery(id+"F0.wireOp",EDGE,"E31.trimOffspring"),sQuery(id+"F0.wireOp",EDGE,"E32.trimOffspring"),sQuery(id+"F0.wireOp",EDGE,"E33.trimOffspring"),sQuery(id+"F0.wireOp",EDGE,"E34"),sQuery(id+"F0.wireOp",EDGE,"E35"),sQuery(id+"F0.wireOp",EDGE,"E36")])],"isStart":false})],"blendedInto":[makeQuery(id+"F1.opExtrude","CAP_FACE",FACE,{"disambiguationData":[OSD([sQuery(id+"F0.wireOp",EDGE,"E1"),sQuery(id+"F0.wireOp",EDGE,"E6"),sQuery(id+"F0.wireOp",EDGE,"E7"),sQuery(id+"F0.wireOp",EDGE,"E8"),sQuery(id+"F0.wireOp",EDGE,"E9"),sQuery(id+"F0.wireOp",EDGE,"E19"),sQuery(id+"F0.wireOp",EDGE,"E20"),subQ0,sQuery(id+"F0.wireOp",EDGE,"E22"),sQuery(id+"F0.wireOp",EDGE,"E23"),sQuery(id+"F0.wireOp",EDGE,"E24"),sQuery(id+"F0.wireOp",EDGE,"E25"),sQuery(id+"F0.wireOp",EDGE,"E26"),sQuery(id+"F0.wireOp",EDGE,"E27"),sQuery(id+"F0.wireOp",EDGE,"E28.trimOffspring"),sQuery(id+"F0.wireOp",EDGE,"E29.trimOffspring"),sQuery(id+"F0.wireOp",EDGE,"E30.trimOffspring"),sQuery(id+"F0.wireOp",EDGE,"E31.trimOffspring"),sQuery(id+"F0.wireOp",EDGE,"E32.trimOffspring"),sQuery(id+"F0.wireOp",EDGE,"E33.trimOffspring"),sQuery(id+"F0.wireOp",EDGE,"E34"),sQuery(id+"F0.wireOp",EDGE,"E35"),sQuery(id+"F0.wireOp",EDGE,"E36")])],"isStart":false})]});}
            var Q31;
            {var subQ0=sQuery(id+"F0.wireOp",EDGE,"E22");Q31=makeQuery(id+"F2.opChamfer","BLEND_EDGE",EDGE,{"blendedFrom":[makeQuery(id+"F1.opExtrude","CAP_EDGE",EDGE,{"disambiguationData":[OSD([subQ0])],"isStart":false}),makeQuery(id+"F1.opExtrude","CAP_FACE",FACE,{"disambiguationData":[OSD([sQuery(id+"F0.wireOp",EDGE,"E1"),sQuery(id+"F0.wireOp",EDGE,"E6"),sQuery(id+"F0.wireOp",EDGE,"E7"),sQuery(id+"F0.wireOp",EDGE,"E8"),sQuery(id+"F0.wireOp",EDGE,"E9"),sQuery(id+"F0.wireOp",EDGE,"E19"),sQuery(id+"F0.wireOp",EDGE,"E20"),sQuery(id+"F0.wireOp",EDGE,"E21"),subQ0,sQuery(id+"F0.wireOp",EDGE,"E23"),sQuery(id+"F0.wireOp",EDGE,"E24"),sQuery(id+"F0.wireOp",EDGE,"E25"),sQuery(id+"F0.wireOp",EDGE,"E26"),sQuery(id+"F0.wireOp",EDGE,"E27"),sQuery(id+"F0.wireOp",EDGE,"E28.trimOffspring"),sQuery(id+"F0.wireOp",EDGE,"E29.trimOffspring"),sQuery(id+"F0.wireOp",EDGE,"E30.trimOffspring"),sQuery(id+"F0.wireOp",EDGE,"E31.trimOffspring"),sQuery(id+"F0.wireOp",EDGE,"E32.trimOffspring"),sQuery(id+"F0.wireOp",EDGE,"E33.trimOffspring"),sQuery(id+"F0.wireOp",EDGE,"E34"),sQuery(id+"F0.wireOp",EDGE,"E35"),sQuery(id+"F0.wireOp",EDGE,"E36")])],"isStart":false})],"blendedInto":[makeQuery(id+"F1.opExtrude","CAP_FACE",FACE,{"disambiguationData":[OSD([sQuery(id+"F0.wireOp",EDGE,"E1"),sQuery(id+"F0.wireOp",EDGE,"E6"),sQuery(id+"F0.wireOp",EDGE,"E7"),sQuery(id+"F0.wireOp",EDGE,"E8"),sQuery(id+"F0.wireOp",EDGE,"E9"),sQuery(id+"F0.wireOp",EDGE,"E19"),sQuery(id+"F0.wireOp",EDGE,"E20"),sQuery(id+"F0.wireOp",EDGE,"E21"),subQ0,sQuery(id+"F0.wireOp",EDGE,"E23"),sQuery(id+"F0.wireOp",EDGE,"E24"),sQuery(id+"F0.wireOp",EDGE,"E25"),sQuery(id+"F0.wireOp",EDGE,"E26"),sQuery(id+"F0.wireOp",EDGE,"E27"),sQuery(id+"F0.wireOp",EDGE,"E28.trimOffspring"),sQuery(id+"F0.wireOp",EDGE,"E29.trimOffspring"),sQuery(id+"F0.wireOp",EDGE,"E30.trimOffspring"),sQuery(id+"F0.wireOp",EDGE,"E31.trimOffspring"),sQuery(id+"F0.wireOp",EDGE,"E32.trimOffspring"),sQuery(id+"F0.wireOp",EDGE,"E33.trimOffspring"),sQuery(id+"F0.wireOp",EDGE,"E34"),sQuery(id+"F0.wireOp",EDGE,"E35"),sQuery(id+"F0.wireOp",EDGE,"E36")])],"isStart":false})]});}
            var Q32;
            {var subQ0=sQuery(id+"F0.wireOp",EDGE,"E22");Q32=makeQuery(id+"F2.opChamfer","BLEND_EDGE",EDGE,{"blendedFrom":[makeQuery(id+"F1.opExtrude","CAP_EDGE",EDGE,{"disambiguationData":[OSD([subQ0])],"isStart":true}),makeQuery(id+"F1.opExtrude","CAP_EDGE",EDGE,{"disambiguationData":[OSD([subQ0])],"isStart":false})],"blendedInto":[]});}
            var Q33;
            {var subQ0=sQuery(id+"F0.wireOp",EDGE,"E22");Q33=makeQuery(id+"F2.opChamfer","BLEND_EDGE",EDGE,{"blendedFrom":[makeQuery(id+"F1.opExtrude","CAP_EDGE",EDGE,{"disambiguationData":[OSD([subQ0])],"isStart":true}),makeQuery(id+"F1.opExtrude","CAP_FACE",FACE,{"disambiguationData":[OSD([sQuery(id+"F0.wireOp",EDGE,"E1"),sQuery(id+"F0.wireOp",EDGE,"E6"),sQuery(id+"F0.wireOp",EDGE,"E7"),sQuery(id+"F0.wireOp",EDGE,"E8"),sQuery(id+"F0.wireOp",EDGE,"E9"),sQuery(id+"F0.wireOp",EDGE,"E19"),sQuery(id+"F0.wireOp",EDGE,"E20"),sQuery(id+"F0.wireOp",EDGE,"E21"),subQ0,sQuery(id+"F0.wireOp",EDGE,"E23"),sQuery(id+"F0.wireOp",EDGE,"E24"),sQuery(id+"F0.wireOp",EDGE,"E25"),sQuery(id+"F0.wireOp",EDGE,"E26"),sQuery(id+"F0.wireOp",EDGE,"E27"),sQuery(id+"F0.wireOp",EDGE,"E28.trimOffspring"),sQuery(id+"F0.wireOp",EDGE,"E29.trimOffspring"),sQuery(id+"F0.wireOp",EDGE,"E30.trimOffspring"),sQuery(id+"F0.wireOp",EDGE,"E31.trimOffspring"),sQuery(id+"F0.wireOp",EDGE,"E32.trimOffspring"),sQuery(id+"F0.wireOp",EDGE,"E33.trimOffspring"),sQuery(id+"F0.wireOp",EDGE,"E34"),sQuery(id+"F0.wireOp",EDGE,"E35"),sQuery(id+"F0.wireOp",EDGE,"E36")])],"isStart":true})],"blendedInto":[makeQuery(id+"F1.opExtrude","CAP_FACE",FACE,{"disambiguationData":[OSD([sQuery(id+"F0.wireOp",EDGE,"E1"),sQuery(id+"F0.wireOp",EDGE,"E6"),sQuery(id+"F0.wireOp",EDGE,"E7"),sQuery(id+"F0.wireOp",EDGE,"E8"),sQuery(id+"F0.wireOp",EDGE,"E9"),sQuery(id+"F0.wireOp",EDGE,"E19"),sQuery(id+"F0.wireOp",EDGE,"E20"),sQuery(id+"F0.wireOp",EDGE,"E21"),subQ0,sQuery(id+"F0.wireOp",EDGE,"E23"),sQuery(id+"F0.wireOp",EDGE,"E24"),sQuery(id+"F0.wireOp",EDGE,"E25"),sQuery(id+"F0.wireOp",EDGE,"E26"),sQuery(id+"F0.wireOp",EDGE,"E27"),sQuery(id+"F0.wireOp",EDGE,"E28.trimOffspring"),sQuery(id+"F0.wireOp",EDGE,"E29.trimOffspring"),sQuery(id+"F0.wireOp",EDGE,"E30.trimOffspring"),sQuery(id+"F0.wireOp",EDGE,"E31.trimOffspring"),sQuery(id+"F0.wireOp",EDGE,"E32.trimOffspring"),sQuery(id+"F0.wireOp",EDGE,"E33.trimOffspring"),sQuery(id+"F0.wireOp",EDGE,"E34"),sQuery(id+"F0.wireOp",EDGE,"E35"),sQuery(id+"F0.wireOp",EDGE,"E36")])],"isStart":true})]});}
            var Q34;
            Q34=makeQuery(id+"F1.opExtrude","CAP_EDGE",EDGE,{"disambiguationData":[OSD([sQuery(id+"F0.wireOp",EDGE,"E29.trimOffspring")])],"isStart":false});
            var Q35;
            Q35=makeQuery(id+"F1.opExtrude","CAP_EDGE",EDGE,{"disambiguationData":[OSD([sQuery(id+"F0.wireOp",EDGE,"E29.trimOffspring")])],"isStart":true});
            chamfer(context, id + "F4", {"entities" : qUnion([Q0, Q1, Q2, Q3, Q4, Q5, Q6, Q7, Q8, Q9, Q10, Q11, Q12, Q13, Q14, Q15, Q16, Q17, Q18, Q19, Q20, Q21, Q22, Q23, Q24, Q25, Q26, Q27, Q28, Q29, Q30, Q31, Q32, Q33, Q34, Q35]), "width" : 1 * mm, "tangentPropagation" : true});
        }
    });
